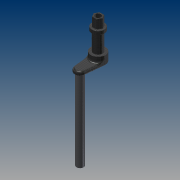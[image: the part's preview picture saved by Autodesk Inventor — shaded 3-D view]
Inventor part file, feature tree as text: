
AUTODESK INVENTOR PART (.ipt)
format: ipt  version: 2014 (Build 180170000, 170)  size: 240,640 bytes
history: native  units: mm
features: extrude x9, sketch x9, fillet x7
ambient origin geometry x8: Origin, YZ Plane, XZ Plane, XY Plane, X Axis, Y Axis, Z Axis, Center Point
bodies: Solid1 (feature_tree)
feature tree (25):
  extrude  "Extrusion1"  Depth=30.0mm TaperAngle=0.0deg
  extrude  "Extrusion2"  Depth=100.0mm TaperAngle=0.0deg
  extrude  "Extrusion3"  Depth=20.0mm TaperAngle=0.0deg
  extrude  "Extrusion4"  Depth=50.0mm TaperAngle=0.0deg
  extrude  "Extrusion5"  Depth=30.0mm
  extrude  "Extrusion6"  Depth=2.0mm
  fillet  "Fillet1"  Radius=2.0mm
  fillet  "Fillet2"  Radius=60.0mm
  extrude  "Extrusion7"  Depth=20.0mm TaperAngle=0.0deg
  fillet  "Fillet3"  Radius=10.0mm
  fillet  "Fillet4"  Radius=5.0mm
  fillet  "Fillet5"  Radius=10.0mm
  extrude  "Extrusion8"  Depth=450.0mm TaperAngle=0.0deg
  extrude  "Extrusion9"  Depth=200.0mm TaperAngle=0.0deg
  fillet  "Fillet6"  Radius=2.0mm
  fillet  "Fillet7"  Radius=5.0mm
  sketch  "Sketch1"  dims[d0=80.0mm d1=30.0mm d2=0.0mm]
  sketch  "Sketch2"  dims[d3=50.0mm d4=100.0mm d5=0.0mm]
  sketch  "Sketch3"  dims[d6=10.0mm d7=20.0mm d8=0.0mm]
  sketch  "Sketch4"  dims[d9=50.0mm d10=50.0mm d11=0.0mm]
  sketch  "Sketch5"  dims[d12=50.0mm d13=0.0mm d14=30.0mm]
  sketch  "Sketch6"  dims[d15=50.0mm d16=0.0mm d17=2.0mm d18=2.0mm d19=60.0mm]
  sketch  "Sketch7"  dims[d20=100.0mm d21=20.0mm d22=0.0mm d23=10.0mm d24=5.0mm d25=10.0mm]
  sketch  "Sketch8"  dims[d26=40.0mm d27=450.0mm d28=0.0mm]
  sketch  "Sketch9"  dims[d29=20.0mm d30=200.0mm d31=0.0mm d32=2.0mm d33=5.0mm]
